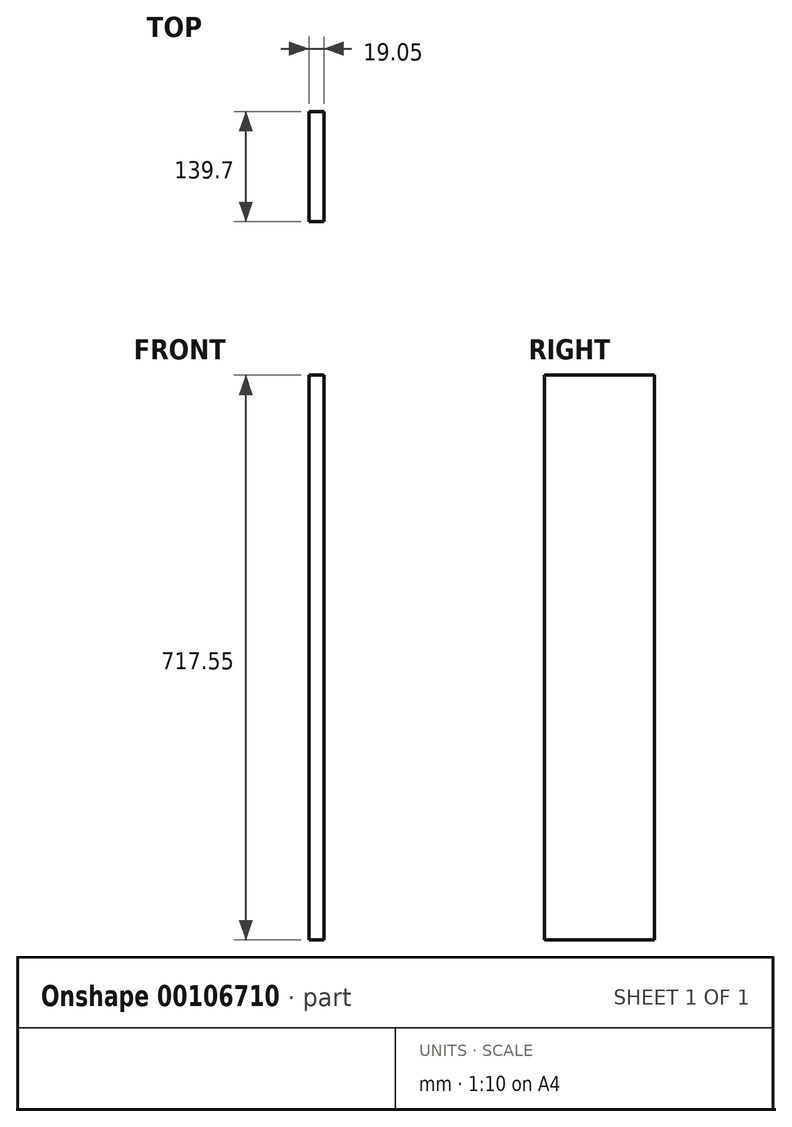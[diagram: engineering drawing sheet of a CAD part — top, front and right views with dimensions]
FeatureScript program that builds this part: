
annotation { "Feature Type Name" : "Feature", "Feature Type Description" : "" }
export const myFeature = defineFeature(function(context is Context, id is Id, definition is map)
    precondition{}
    {
        {
            var Q0;
            Q0=qCreatedBy(makeId("Right.planeOp"),FACE);
            var sketch = newSketch(context, id + "F0", { "sketchPlane" : qUnion([Q0])});
            skLineSegment(sketch, "E0.bottom", {"start": v(0, 0) * mm, "end": v(139.7, 0) * mm});
            skLineSegment(sketch, "E0.top", {"start": v(0, 717.55) * mm, "end": v(139.7, 717.55) * mm});
            skLineSegment(sketch, "E0.left", {"start": v(0, 0) * mm, "end": v(0, 717.55) * mm});
            skLineSegment(sketch, "E0.right", {"start": v(139.7, 0) * mm, "end": v(139.7, 717.55) * mm});
            skSolve(sketch);
        }
        {
            var Q0;
            Q0=makeQuery(id+"F0.imprint","IMPRINT",FACE,{"disambiguationData":[TD([[makeQuery(id+"F0.imprint","IMPRINT",EDGE,{"derivedFrom":sQuery(id+"F0.wireOp",EDGE,"E0.bottom")}),1.0]])]});
            extrude(context, id + "F1", {"entities" : qUnion([Q0]), "depth" : 19.05 * mm});
        }
    });
